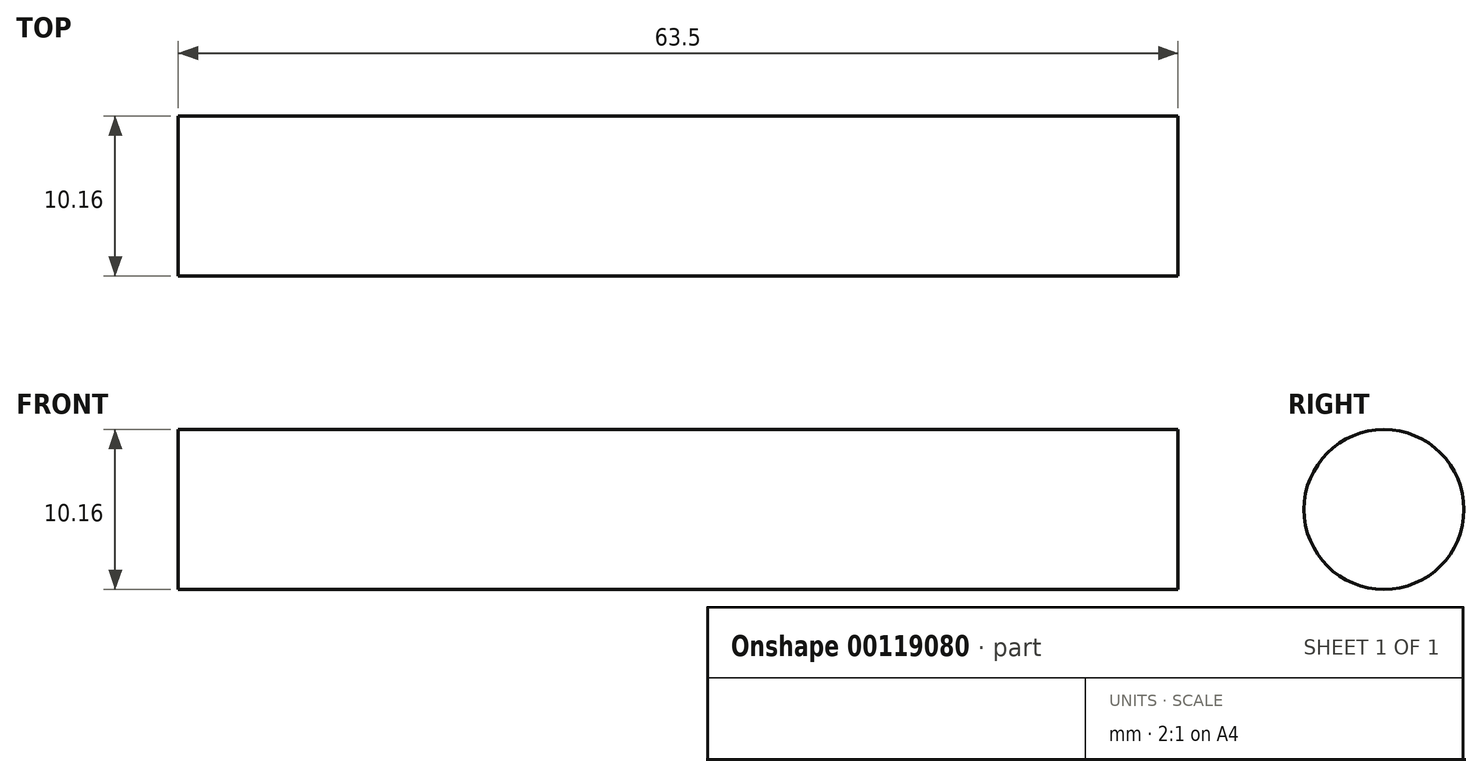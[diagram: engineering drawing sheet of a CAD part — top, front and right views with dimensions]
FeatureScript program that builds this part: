
annotation { "Feature Type Name" : "Feature", "Feature Type Description" : "" }
export const myFeature = defineFeature(function(context is Context, id is Id, definition is map)
    precondition{}
    {
        {
            var Q0;
            Q0=qCreatedBy(makeId("Right.planeOp"),FACE);
            var sketch = newSketch(context, id + "F0", { "sketchPlane" : qUnion([Q0])});
            skCircle(sketch, "E0", {"center": v(0, 0) * mm, "radius": 5.08 * mm});
            skSolve(sketch);
        }
        {
            var Q0;
            Q0 = qSketchRegion(id + "F0", true);
            extrude(context, id + "F1", {"entities" : qUnion([Q0]), "depth" : 63.5 * mm});
        }
    });
